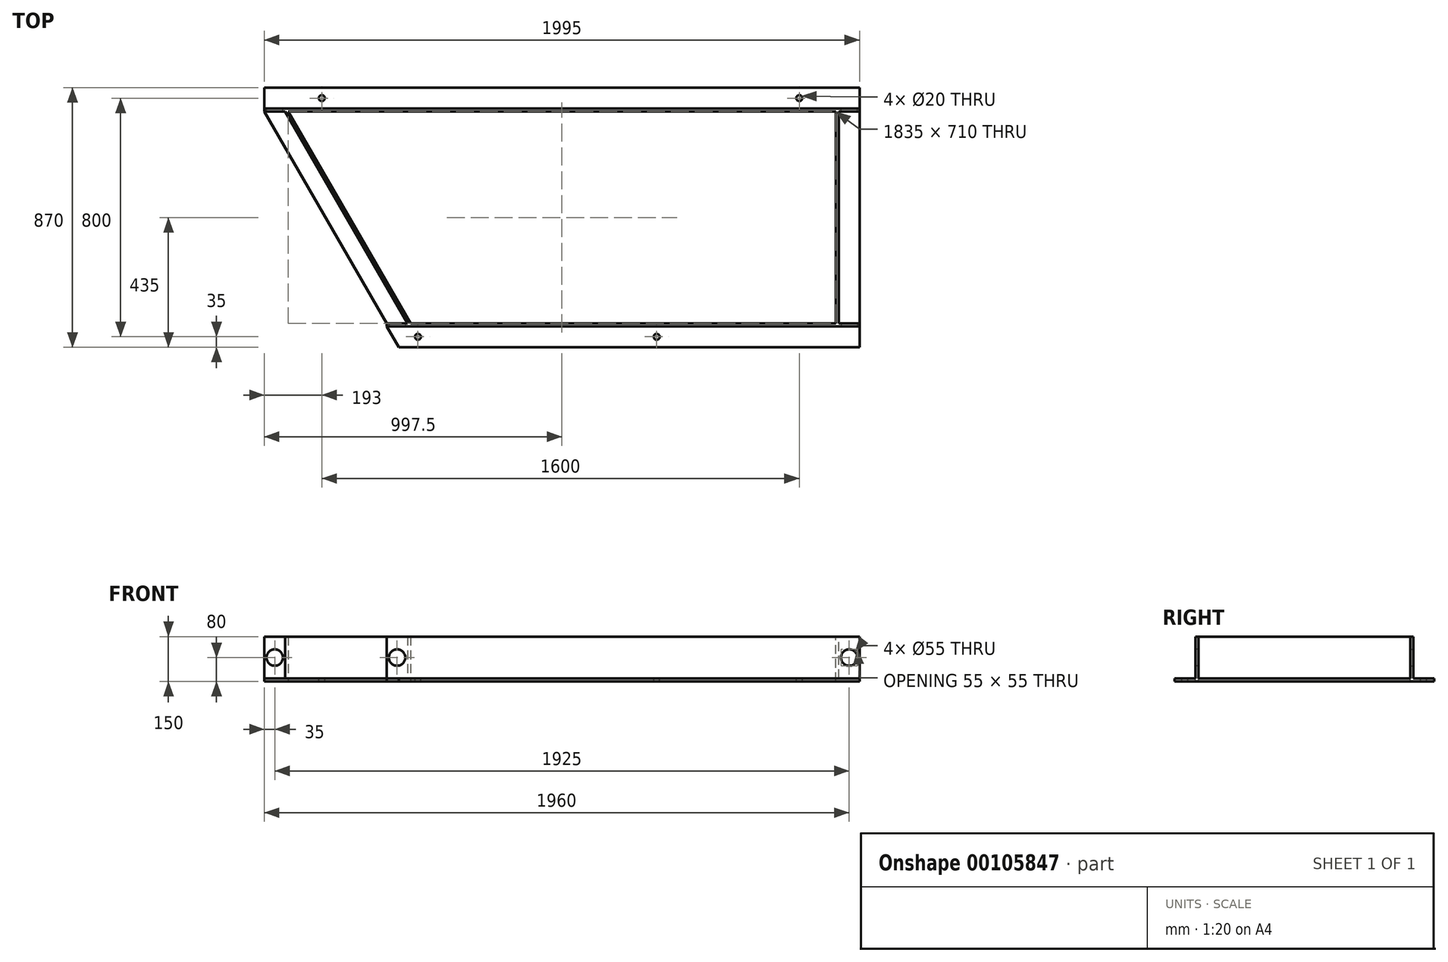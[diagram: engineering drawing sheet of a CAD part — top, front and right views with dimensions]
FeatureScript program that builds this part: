
annotation { "Feature Type Name" : "Feature", "Feature Type Description" : "" }
export const myFeature = defineFeature(function(context is Context, id is Id, definition is map)
    precondition{}
    {
        {
            var Q0;
            Q0=qCreatedBy(makeId("Right.planeOp"),FACE);
            var sketch = newSketch(context, id + "F0", { "sketchPlane" : qUnion([Q0])});
            skLineSegment(sketch, "E0.bottom", {"start": v(0, 0) * mm, "end": v(10, 0) * mm});
            skLineSegment(sketch, "E0.top", {"start": v(0, 150) * mm, "end": v(10, 150) * mm});
            skLineSegment(sketch, "E0.left", {"start": v(0, 0) * mm, "end": v(0, 150) * mm});
            skLineSegment(sketch, "E0.right", {"start": v(10, 10) * mm, "end": v(10, 150) * mm});
            skLineSegment(sketch, "E1.bottom", {"start": v(0, 0) * mm, "end": v(80, 0) * mm});
            skLineSegment(sketch, "E1.top", {"start": v(10, 10) * mm, "end": v(80, 10) * mm});
            skLineSegment(sketch, "E1.left", {"start": v(0, 0) * mm, "end": v(0, 10) * mm});
            skLineSegment(sketch, "E1.right", {"start": v(80, 0) * mm, "end": v(80, 10) * mm});
            skSolve(sketch);
        }
        {
            var Q0;
            Q0 = qSketchRegion(id + "F0", true);
            extrude(context, id + "F1", {"entities" : qUnion([Q0]), "depth" : 1995 * mm});
        }
        {
            var Q0;
            Q0=makeQuery(id+"F1.opExtrude","SWEPT_FACE",FACE,{"disambiguationData":[OSD([sQuery(id+"F0.wireOp",EDGE,"E0.left"),sQuery(id+"F0.wireOp",EDGE,"E1.left")])]});
            var sketch = newSketch(context, id + "F2", { "sketchPlane" : qUnion([Q0])});
            skLineSegment(sketch, "E2.bottom", {"start": v(1915, 0) * mm, "end": v(1925, 0) * mm});
            skLineSegment(sketch, "E2.top", {"start": v(1915, 150) * mm, "end": v(1925, 150) * mm});
            skLineSegment(sketch, "E2.left", {"start": v(1915, 0) * mm, "end": v(1915, 150) * mm});
            skLineSegment(sketch, "E2.right", {"start": v(1925, 10) * mm, "end": v(1925, 150) * mm});
            skLineSegment(sketch, "E3.bottom", {"start": v(1915, 0) * mm, "end": v(1995, 0) * mm});
            skLineSegment(sketch, "E3.top", {"start": v(1925, 10) * mm, "end": v(1995, 10) * mm});
            skLineSegment(sketch, "E3.left", {"start": v(1915, 0) * mm, "end": v(1915, 10) * mm});
            skLineSegment(sketch, "E3.right", {"start": v(1995, 0) * mm, "end": v(1995, 10) * mm});
            skSolve(sketch);
        }
        {
            var Q0;
            Q0 = qSketchRegion(id + "F2", true);
            extrude(context, id + "F3", {"entities" : qUnion([Q0]), "operationType" : NewBodyOperationType.ADD, "depth" : 710 * mm});
        }
        {
            var Q0;
            Q0=makeQuery(id+"F3.boolean.opBoolean","MERGE",FACE,{"derivedFrom":[makeQuery(id+"F1.opExtrude","CAP_FACE",FACE,{"disambiguationData":[OSD([sQuery(id+"F0.wireOp",EDGE,"E0.top"),sQuery(id+"F0.wireOp",EDGE,"E0.left"),sQuery(id+"F0.wireOp",EDGE,"E0.right"),sQuery(id+"F0.wireOp",EDGE,"E1.bottom"),sQuery(id+"F0.wireOp",EDGE,"E1.top"),sQuery(id+"F0.wireOp",EDGE,"E1.left"),sQuery(id+"F0.wireOp",EDGE,"E1.right")])],"isStart":false}),makeQuery(id+"F3.opExtrude","SWEPT_FACE",FACE,{"disambiguationData":[OSD([sQuery(id+"F2.wireOp",EDGE,"E3.right")])]})]});
            var sketch = newSketch(context, id + "F4", { "sketchPlane" : qUnion([Q0])});
            skLineSegment(sketch, "E4.bottom", {"start": v(-720, 10) * mm, "end": v(-790, 10) * mm});
            skLineSegment(sketch, "E4.top", {"start": v(-710, 0) * mm, "end": v(-790, 0) * mm});
            skLineSegment(sketch, "E4.left", {"start": v(-710, 10) * mm, "end": v(-710, 0) * mm});
            skLineSegment(sketch, "E4.right", {"start": v(-790, 10) * mm, "end": v(-790, 0) * mm});
            skLineSegment(sketch, "E5.bottom", {"start": v(-710, 0) * mm, "end": v(-720, 0) * mm});
            skLineSegment(sketch, "E5.top", {"start": v(-710, 150) * mm, "end": v(-720, 150) * mm});
            skLineSegment(sketch, "E5.left", {"start": v(-710, 0) * mm, "end": v(-710, 150) * mm});
            skLineSegment(sketch, "E5.right", {"start": v(-720, 10) * mm, "end": v(-720, 150) * mm});
            skSolve(sketch);
        }
        {
            var Q0;
            Q0 = qSketchRegion(id + "F4", true);
            extrude(context, id + "F5", {"entities" : qUnion([Q0]), "oppositeDirection" : true, "depth" : 1585 * mm});
        }
        {
            var Q0;
            Q0=qCreatedBy(makeId("Top.planeOp"),FACE);
            var sketch = newSketch(context, id + "F6", { "sketchPlane" : qUnion([Q0])});
            skLineSegment(sketch, "E6", {"start": v(80, 0) * mm, "end": v(490, -710) * mm});
            skLineSegment(sketch, "E7", {"start": v(80, 0) * mm, "end": v(0, 0) * mm});
            skLineSegment(sketch, "E8", {"start": v(0, 0) * mm, "end": v(410, -710) * mm});
            skLineSegment(sketch, "E9", {"start": v(410, -710) * mm, "end": v(490, -710) * mm});
            skSolve(sketch);
        }
        {
            var Q0;
            Q0 = qSketchRegion(id + "F6", true);
            extrude(context, id + "F7", {"entities" : qUnion([Q0]), "depth" : 10 * mm});
        }
        {
            var Q0;
            Q0=makeQuery(id+"F7.opExtrude","CAP_FACE",FACE,{"disambiguationData":[OSD([sQuery(id+"F6.wireOp",EDGE,"E6"),sQuery(id+"F6.wireOp",EDGE,"E7"),sQuery(id+"F6.wireOp",EDGE,"E8"),sQuery(id+"F6.wireOp",EDGE,"E9")])],"isStart":false});
            var sketch = newSketch(context, id + "F8", { "sketchPlane" : qUnion([Q0])});
            skLineSegment(sketch, "E10", {"start": v(80, 0) * mm, "end": v(490, -710) * mm});
            skLineSegment(sketch, "E11", {"start": v(490, -710) * mm, "end": v(480, -710) * mm});
            skLineSegment(sketch, "E12", {"start": v(480, -710) * mm, "end": v(70, 0) * mm});
            skLineSegment(sketch, "E13", {"start": v(70, 0) * mm, "end": v(80, 0) * mm});
            skSolve(sketch);
        }
        {
            var Q0;
            Q0 = qSketchRegion(id + "F8", true);
            extrude(context, id + "F9", {"entities" : qUnion([Q0]), "operationType" : NewBodyOperationType.ADD, "depth" : 140 * mm});
        }
        {
            var Q0;
            Q0=makeQuery(id+"F5.opExtrude","SWEPT_FACE",FACE,{"disambiguationData":[OSD([sQuery(id+"F4.wireOp",EDGE,"E4.bottom")])]});
            var sketch = newSketch(context, id + "F10", { "sketchPlane" : qUnion([Q0])});
            skCircle(sketch, "E14", {"center": v(515, -755) * mm, "radius": 10 * mm});
            skCircle(sketch, "E15", {"center": v(1315, -755) * mm, "radius": 10 * mm});
            skCircle(sketch, "E16", {"center": v(1793, 45) * mm, "radius": 10 * mm});
            skCircle(sketch, "E17", {"center": v(193, 45) * mm, "radius": 10 * mm});
            skSolve(sketch);
        }
        {
            var Q0;
            Q0 = qSketchRegion(id + "F10", true);
            extrude(context, id + "F11", {"entities" : qUnion([Q0]), "operationType" : NewBodyOperationType.REMOVE, "oppositeDirection" : true, "depth" : 25 * mm});
        }
        {
            var Q0;
            Q0=makeQuery(id+"F5.opExtrude","SWEPT_FACE",FACE,{"disambiguationData":[OSD([sQuery(id+"F4.wireOp",EDGE,"E5.right")])]});
            var sketch = newSketch(context, id + "F12", { "sketchPlane" : qUnion([Q0])});
            skCircle(sketch, "E18", {"center": v(445, 80) * mm, "radius": 27.5 * mm});
            skCircle(sketch, "E19", {"center": v(1960, 80) * mm, "radius": 27.5 * mm});
            skSolve(sketch);
        }
        {
            var Q0;
            Q0 = qSketchRegion(id + "F12", true);
            extrude(context, id + "F13", {"entities" : qUnion([Q0]), "operationType" : NewBodyOperationType.REMOVE, "oppositeDirection" : true, "depth" : 15 * mm});
        }
        {
            var Q0;
            Q0=makeQuery(id+"F1.opExtrude","SWEPT_FACE",FACE,{"disambiguationData":[OSD([sQuery(id+"F0.wireOp",EDGE,"E0.right")])]});
            var sketch = newSketch(context, id + "F14", { "sketchPlane" : qUnion([Q0])});
            skCircle(sketch, "E20", {"center": v(-1960, 80) * mm, "radius": 27.5 * mm});
            skCircle(sketch, "E21", {"center": v(-35, 80) * mm, "radius": 27.5 * mm});
            skSolve(sketch);
        }
        {
            var Q0;
            Q0 = qSketchRegion(id + "F14", true);
            extrude(context, id + "F15", {"entities" : qUnion([Q0]), "operationType" : NewBodyOperationType.REMOVE, "oppositeDirection" : true, "depth" : 25 * mm});
        }
        {
            var Q0;
            Q0=makeQuery(id+"F5.opExtrude","SWEPT_FACE",FACE,{"disambiguationData":[OSD([sQuery(id+"F4.wireOp",EDGE,"E4.bottom")])]});
            var sketch = newSketch(context, id + "F16", { "sketchPlane" : qUnion([Q0])});
            skLineSegment(sketch, "E22", {"start": v(410, -720) * mm, "end": v(450.42, -790) * mm});
            skLineSegment(sketch, "E23", {"start": v(450.42, -790) * mm, "end": v(410, -790) * mm});
            skLineSegment(sketch, "E24", {"start": v(410, -790) * mm, "end": v(410, -720) * mm});
            skSolve(sketch);
        }
        {
            var Q0;
            Q0 = qSketchRegion(id + "F16", true);
            extrude(context, id + "F17", {"entities" : qUnion([Q0]), "operationType" : NewBodyOperationType.REMOVE, "oppositeDirection" : true, "depth" : 25 * mm});
        }
    });
